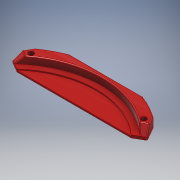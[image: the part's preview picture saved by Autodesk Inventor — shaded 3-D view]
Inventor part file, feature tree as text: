
AUTODESK INVENTOR PART (.ipt)
format: ipt  version: 2018 (Build 220112000, 112)  size: 291,840 bytes
history: native  units: mm
features: fillet x11, extrude x3, sketch x3, chamfer x2, hole x1
ambient origin geometry x8: Origin, YZ Plane, XZ Plane, XY Plane, X Axis, Y Axis, Z Axis, Center Point
bodies: Solid1 (feature_tree)
feature tree (20):
  extrude  "Extrusion1"  Depth=334.0mm
  extrude  "Extrusion2"  TaperAngle=150.0deg  [1 undecoded]
  extrude  "Extrusion3"  TaperAngle=30.0deg  [1 undecoded]
  hole  "Hole1"  [1 undecoded]
  chamfer  "Chamfer1"  Angle=60.0deg  [1 undecoded]
  chamfer  "Chamfer2"  Distance=30.0mm
  fillet  "Fillet1"  [1 undecoded]
  fillet  "Fillet2"  Radius=3.0mm
  fillet  "Fillet3"  Radius=21.5mm
  fillet  "Fillet4"  [1 undecoded]
  fillet  "Fillet5"  Radius=30.0mm
  fillet  "Fillet6"  Radius=21.5mm
  fillet  "Fillet7"  [1 undecoded]
  fillet  "Fillet8"  Radius=30.0mm
  fillet  "Fillet9"  [1 undecoded]
  fillet  "Fillet10"  Radius=2.0mm
  fillet  "Fillet11"  Radius=208.768749mm
  sketch  "Sketch2"  dims[d0=312.0mm d1=334.0mm]
  sketch  "Sketch3"  dims[d3=21.5mm d4=150.0deg]
  sketch  "Sketch5"  dims[d5=21.5mm d6=30.0deg d8=30.0mm d9=60.0deg d10=30.0mm d11=120.0deg d13=3.0mm d14=0.0mm d18=21.5mm d19=150.0deg d20=30.0mm d21=21.5mm d22=30.0deg d23=30.0mm d24=120.0deg d26=2.0mm d27=0.0mm d32=208.768749mm d33=134.029613mm d36=30.0mm d40=30.0mm d43=13.0mm d44=0.0mm d46=156.0mm d47=23.038346mm d48=21.5mm d49=150.0deg d50=11.0mm d51=156.0mm d52=21.5mm d53=28.274334mm d54=11.0mm d55=10.75mm d56=10.0mm d57=10.75mm d58=10.0mm d59=10.0mm d60=10.0mm d61=5.0mm d62=6.0mm d63=10.0mm d64=13.0mm d65=90.0deg d66=18.0mm d67=0.0mm d68=13.0mm d69=2.0mm d70=45.0deg d71=13.0mm d72=2.0mm d73=45.0deg d74=2.0mm d75=2.0mm d76=2.0mm d77=2.0mm d78=2.0mm d79=2.0mm d80=2.0mm d81=2.0mm d82=2.0mm d83=2.0mm d84=2.0mm]
note: 8 required parameter values undecoded (feature->parameter linkage not recoverable at this tier; creation-order binding heuristic only, values carry confidence <= 0.55)
